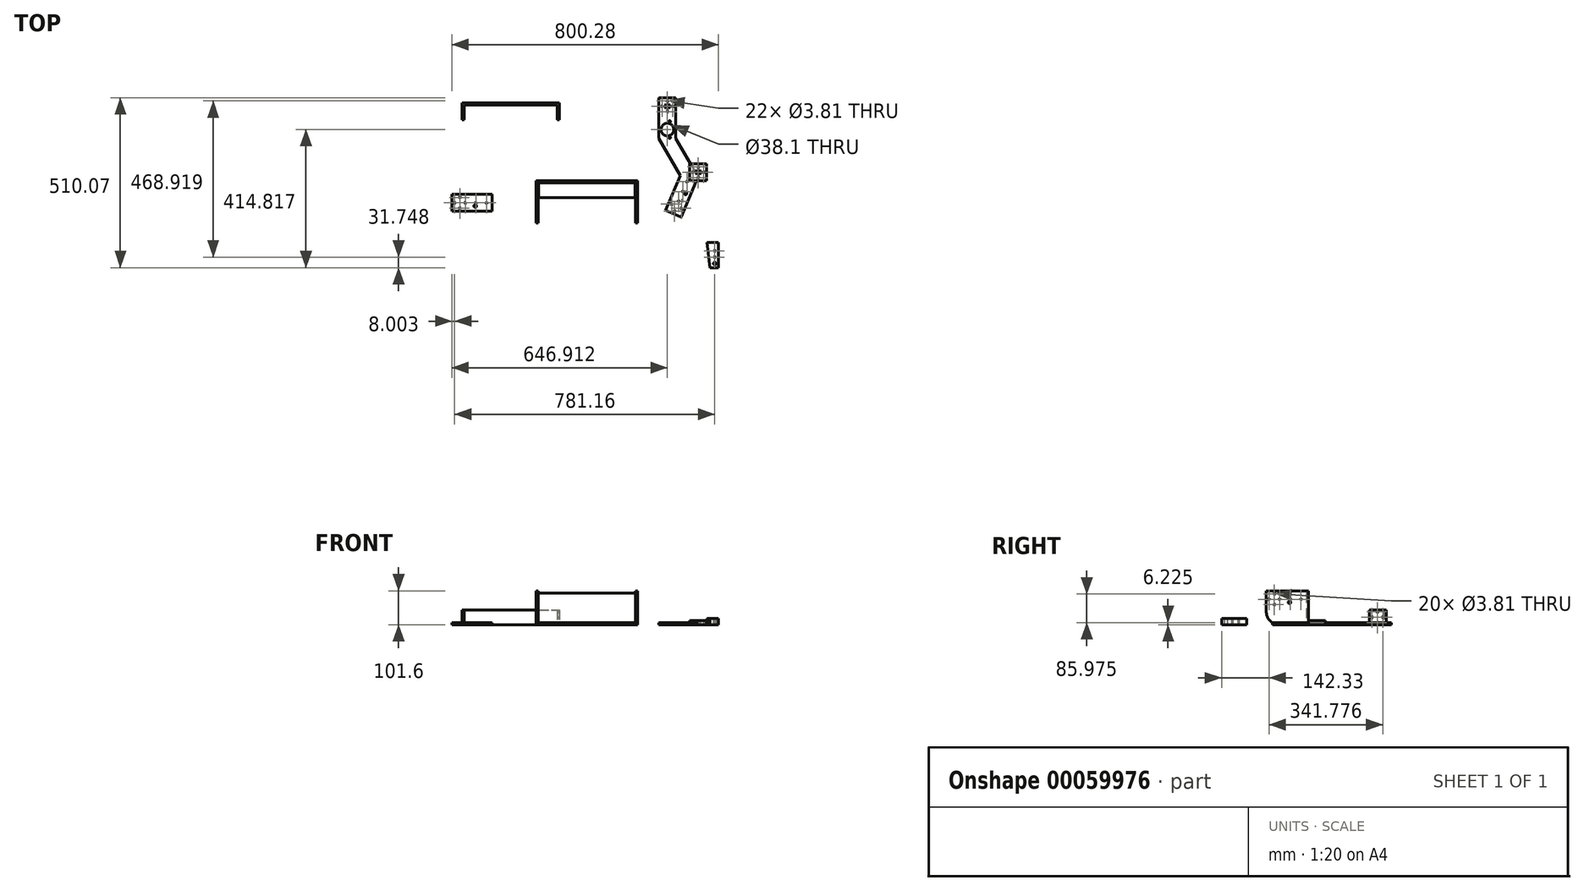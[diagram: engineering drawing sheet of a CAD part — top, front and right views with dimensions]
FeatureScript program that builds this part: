
annotation { "Feature Type Name" : "Feature", "Feature Type Description" : "" }
export const myFeature = defineFeature(function(context is Context, id is Id, definition is map)
    precondition{}
    {
        {
            var Q0;
            Q0=qCreatedBy(makeId("Top.planeOp"),FACE);
            var sketch = newSketch(context, id + "F0", { "sketchPlane" : qUnion([Q0])});
            skLineSegment(sketch, "E0.bottom", {"start": v(-92.72, 248.74) * mm, "end": v(-41.92, 248.74) * mm});
            skLineSegment(sketch, "E0.left", {"start": v(-92.72, 248.74) * mm, "end": v(-92.72, 70.94) * mm});
            skLineSegment(sketch, "E0.right", {"start": v(-41.92, 248.74) * mm, "end": v(-41.92, 127.1) * mm});
            skPoint(sketch, "E1.centerSnap0", {"position": v(-67.32, 248.74) * mm});
            skCircle(sketch, "E2", {"center": v(-67.32, 153.49) * mm, "radius": 19.05 * mm});
            skCircle(sketch, "E3", {"center": v(-67.32, 239.34) * mm, "radius": 1.9 * mm});
            skLineSegment(sketch, "E4", {"start": v(-67.32, 153.49) * mm, "end": v(-41.92, 153.49) * mm, "construction": true});
            skCircle(sketch, "E5", {"center": v(-60.82, 177.49) * mm, "radius": 2.7 * mm});
            skCircle(sketch, "E6.MirrorC", {"center": v(-60.82, 129.49) * mm, "radius": 2.7 * mm});
            skCircle(sketch, "E7.1.0", {"center": v(-83.32, 223.34) * mm, "radius": 1.9 * mm});
            skCircle(sketch, "E7.2.0", {"center": v(-67.32, 207.34) * mm, "radius": 1.9 * mm});
            skCircle(sketch, "E7.3.0", {"center": v(-51.32, 223.34) * mm, "radius": 1.9 * mm});
            skPoint(sketch, "E7.center", {"position": v(-67.32, 223.34) * mm});
            skLineSegment(sketch, "E8", {"start": v(14.65, -13.3) * mm, "end": v(14.65, -13.3) * mm});
            skLineSegment(sketch, "E9", {"start": v(14.65, -13.3) * mm, "end": v(-25.75, -108.67) * mm});
            skLineSegment(sketch, "E10", {"start": v(-25.75, -108.67) * mm, "end": v(-72.52, -88.86) * mm});
            skLineSegment(sketch, "E11", {"start": v(14.65, -13.3) * mm, "end": v(14.65, -108.56) * mm, "construction": true});
            skLineSegment(sketch, "E12", {"start": v(-72.52, -88.86) * mm, "end": v(-48.43, -31.97) * mm});
            skLineSegment(sketch, "E13", {"start": v(-48.43, -31.97) * mm, "end": v(-42.25, -17.39) * mm});
            skLineSegment(sketch, "E14", {"start": v(14.65, -13.3) * mm, "end": v(18.79, -3.55) * mm});
            skLineSegment(sketch, "E15", {"start": v(-42.25, -17.39) * mm, "end": v(-28.58, 14.87) * mm});
            skCircle(sketch, "E16.cCircle", {"center": v(-67.32, 223.34) * mm, "radius": 6.35 * mm, "construction": true});
            skLineSegment(sketch, "E16.0", {"start": v(-70.98, 229.69) * mm, "end": v(-63.65, 229.69) * mm});
            skLineSegment(sketch, "E16.1", {"start": v(-63.65, 229.69) * mm, "end": v(-59.99, 223.34) * mm});
            skLineSegment(sketch, "E16.2", {"start": v(-59.99, 223.34) * mm, "end": v(-63.65, 216.99) * mm});
            skLineSegment(sketch, "E16.3", {"start": v(-63.65, 216.99) * mm, "end": v(-70.98, 216.99) * mm});
            skLineSegment(sketch, "E16.4", {"start": v(-70.98, 216.99) * mm, "end": v(-74.65, 223.34) * mm});
            skLineSegment(sketch, "E16.5", {"start": v(-74.65, 223.34) * mm, "end": v(-70.98, 229.69) * mm});
            skPoint(sketch, "E16.0.midPoint", {"position": v(-67.32, 229.69) * mm});
            skLineSegment(sketch, "E17", {"start": v(-28.58, 14.87) * mm, "end": v(-28.58, 14.87) * mm});
            skLineSegment(sketch, "E18", {"start": v(-28.58, 14.87) * mm, "end": v(-92.72, 127.1) * mm});
            skLineSegment(sketch, "E19", {"start": v(-41.92, 127.1) * mm, "end": v(24.73, 10.48) * mm});
            skLineSegment(sketch, "E20", {"start": v(24.73, 10.48) * mm, "end": v(18.79, -3.55) * mm});
            skPoint(sketch, "E21.start.orphan", {"position": v(-92.72, 102.69) * mm});
            skPoint(sketch, "E22.orphan", {"position": v(-41.92, 102.69) * mm});
            skSolve(sketch);
        }
        {
            var Q0;
            {var subQ0=sQuery(id+"F0.wireOp",EDGE,"9e544ab8-24b0-4bfb-8a0b-cb48c2a7bfe7.right");Q0=makeQuery(id+"F0.imprint","IMPRINT",FACE,{"disambiguationData":[TD([[makeQuery(id+"F0.imprint","IMPRINT",EDGE,{"derivedFrom":subQ0}),-1.0]])]});}
            var Q1;
            {var subQ6=sQuery(id+"F0.wireOp",EDGE,"E0.bottom");Q1=makeQuery(id+"F0.imprint","IMPRINT",FACE,{"disambiguationData":[TD([[makeQuery(id+"F0.imprint","IMPRINT",EDGE,{"derivedFrom":subQ6}),-1.0]])]});}
            var Q2;
            {var subQ5=sQuery(id+"F0.wireOp",EDGE,"rFdDuM6M-3oRl-HpnY-bc0J-Wi5shL16RlnQ");Q2=makeQuery(id+"F0.imprint","IMPRINT",FACE,{"disambiguationData":[TD([[makeQuery(id+"F0.imprint","IMPRINT",EDGE,{"derivedFrom":subQ5}),-1.0]])]});}
            var Q3;
            {var subQ0=sQuery(id+"F0.wireOp",EDGE,"E10");Q3=makeQuery(id+"F0.imprint","IMPRINT",FACE,{"disambiguationData":[TD([[makeQuery(id+"F0.imprint","IMPRINT",EDGE,{"derivedFrom":subQ0}),-1.0]])]});}
            var Q4;
            {var subQ0=sQuery(id+"F0.wireOp",EDGE,"00836efd-f910-459f-9125-7ec244fb97d2.trimOffspring");Q4=makeQuery(id+"F0.imprint","IMPRINT",FACE,{"disambiguationData":[TD([[makeQuery(id+"F0.imprint","IMPRINT",EDGE,{"derivedFrom":subQ0}),-1.0]])]});}
            extrude(context, id + "F1", {"entities" : qUnion([Q0, Q1, Q2, Q3, Q4]), "depth" : 6.35 * mm});
        }
        {
            var Q0;
            Q0=qCreatedBy(makeId("Top.planeOp"),FACE);
            var sketch = newSketch(context, id + "F2", { "sketchPlane" : qUnion([Q0])});
            skLineSegment(sketch, "E23.bottom", {"start": v(0, 0) * mm, "end": v(50.8, 0) * mm});
            skLineSegment(sketch, "E23.top", {"start": v(0, 50.8) * mm, "end": v(50.8, 50.8) * mm});
            skLineSegment(sketch, "E23.left", {"start": v(0, 0) * mm, "end": v(0, 50.8) * mm});
            skLineSegment(sketch, "E23.right", {"start": v(50.8, 0) * mm, "end": v(50.8, 50.8) * mm});
            skCircle(sketch, "E24.cCircle", {"center": v(25.4, 25.4) * mm, "radius": 6.35 * mm, "construction": true});
            skPoint(sketch, "E24.cCircle.centerSnap0", {"position": v(0, 25.4) * mm});
            skPoint(sketch, "E24.cCircle.centerSnap1", {"position": v(25.4, 0) * mm});
            skLineSegment(sketch, "E24.0", {"start": v(21.73, 31.75) * mm, "end": v(29.07, 31.75) * mm});
            skLineSegment(sketch, "E24.1", {"start": v(29.07, 31.75) * mm, "end": v(32.73, 25.4) * mm});
            skLineSegment(sketch, "E24.2", {"start": v(32.73, 25.4) * mm, "end": v(29.07, 19.05) * mm});
            skLineSegment(sketch, "E24.3", {"start": v(29.07, 19.05) * mm, "end": v(21.73, 19.05) * mm});
            skLineSegment(sketch, "E24.4", {"start": v(21.73, 19.05) * mm, "end": v(18.07, 25.4) * mm});
            skLineSegment(sketch, "E24.5", {"start": v(18.07, 25.4) * mm, "end": v(21.73, 31.75) * mm});
            skPoint(sketch, "E24.0.midPoint", {"position": v(25.4, 31.75) * mm});
            skCircle(sketch, "E25", {"center": v(25.4, 41.4) * mm, "radius": 1.9 * mm});
            skCircle(sketch, "E26.1.0", {"center": v(9.4, 25.4) * mm, "radius": 1.9 * mm});
            skCircle(sketch, "E26.2.0", {"center": v(25.4, 9.4) * mm, "radius": 1.9 * mm});
            skCircle(sketch, "E26.3.0", {"center": v(41.4, 25.4) * mm, "radius": 1.9 * mm});
            skSolve(sketch);
        }
        {
            var Q0;
            Q0=makeQuery(id+"F2.imprint","IMPRINT",FACE,{"disambiguationData":[TD([[makeQuery(id+"F2.imprint","IMPRINT",EDGE,{"derivedFrom":sQuery(id+"F2.wireOp",EDGE,"E23.bottom")}),1.0]])]});
            extrude(context, id + "F3", {"entities" : qUnion([Q0]), "depth" : 12.7 * mm});
        }
        {
            var Q0;
            Q0=qCreatedBy(makeId("Top.planeOp"),FACE);
            var sketch = newSketch(context, id + "F4", { "sketchPlane" : qUnion([Q0])});
            skLineSegment(sketch, "E27.bottom", {"start": v(35.25, -261.33) * mm, "end": v(86.05, -261.33) * mm});
            skLineSegment(sketch, "E27.top", {"start": v(35.25, -185.13) * mm, "end": v(86.05, -185.13) * mm});
            skLineSegment(sketch, "E27.left", {"start": v(35.25, -261.33) * mm, "end": v(35.25, -185.13) * mm});
            skLineSegment(sketch, "E27.right", {"start": v(86.05, -261.33) * mm, "end": v(86.05, -185.13) * mm});
            skCircle(sketch, "E28", {"center": v(74.93, -248.63) * mm, "radius": 3.97 * mm});
            skCircle(sketch, "E29", {"center": v(74.93, -229.58) * mm, "radius": 1.9 * mm});
            skCircle(sketch, "E30", {"center": v(74.93, -210.53) * mm, "radius": 1.9 * mm});
            skLineSegment(sketch, "E31", {"start": v(60.65, -261.33) * mm, "end": v(51.96, -185.13) * mm});
            skSolve(sketch);
        }
        {
            var Q0;
            {var subQ0=sQuery(id+"F4.wireOp",EDGE,"E27.right");Q0=makeQuery(id+"F4.imprint","IMPRINT",FACE,{"disambiguationData":[TD([[makeQuery(id+"F4.imprint","IMPRINT",EDGE,{"derivedFrom":subQ0}),1.0]])]});}
            extrude(context, id + "F5", {"entities" : qUnion([Q0]), "depth" : 19.05 * mm});
        }
        {
            var Q0;
            Q0=qCreatedBy(makeId("Front.planeOp"),FACE);
            var sketch = newSketch(context, id + "F6", { "sketchPlane" : qUnion([Q0])});
            skLineSegment(sketch, "E32.bottom", {"start": v(-156.94, 0) * mm, "end": v(-461.74, 0) * mm});
            skLineSegment(sketch, "E32.top", {"start": v(-156.94, 101.6) * mm, "end": v(-461.74, 101.6) * mm});
            skLineSegment(sketch, "E32.left", {"start": v(-156.94, 0) * mm, "end": v(-156.94, 101.6) * mm});
            skLineSegment(sketch, "E32.right", {"start": v(-461.74, 0) * mm, "end": v(-461.74, 101.6) * mm});
            skLineSegment(sketch, "E33.bottom", {"start": v(-461.74, 101.6) * mm, "end": v(-455.4, 101.6) * mm});
            skLineSegment(sketch, "E33.top", {"start": v(-461.74, 0) * mm, "end": v(-455.4, 0) * mm});
            skLineSegment(sketch, "E33.left", {"start": v(-461.74, 101.6) * mm, "end": v(-461.74, 0) * mm});
            skLineSegment(sketch, "E34.bottom", {"start": v(-156.94, 0) * mm, "end": v(-163.3, 0) * mm});
            skLineSegment(sketch, "E34.top", {"start": v(-156.94, 101.6) * mm, "end": v(-163.3, 101.6) * mm});
            skSolve(sketch);
        }
        {
            var Q0;
            Q0=makeQuery(id+"F6.imprint","IMPRINT",FACE,{"disambiguationData":[TD([[makeQuery(id+"F6.imprint","IMPRINT",EDGE,{"derivedFrom":sQuery(id+"F6.wireOp",EDGE,"E32.bottom")}),-1.0]])]});
            var Q1;
            Q1=makeQuery(id+"F6.imprint","IMPRINT",FACE,{"disambiguationData":[TD([[makeQuery(id+"F6.imprint","IMPRINT",EDGE,{"derivedFrom":sQuery(id+"F6.wireOp",EDGE,"E33.bottom")}),-1.0]])]});
            var Q2;
            Q2=makeQuery(id+"F6.imprint","IMPRINT",FACE,{"disambiguationData":[TD([[makeQuery(id+"F6.imprint","IMPRINT",EDGE,{"derivedFrom":sQuery(id+"F6.wireOp",EDGE,"E34.bottom")}),-1.0]])]});
            extrude(context, id + "F7", {"entities" : qUnion([Q0, Q1, Q2]), "depth" : 6.35 * mm});
        }
        {
            var Q0;
            Q0=makeQuery(id+"F7.opExtrude","CAP_FACE",FACE,{"disambiguationData":[OSD([sQuery(id+"F6.wireOp",EDGE,"E32.bottom"),sQuery(id+"F6.wireOp",EDGE,"E32.top"),sQuery(id+"F6.wireOp",EDGE,"E33.bottom"),sQuery(id+"F6.wireOp",EDGE,"E33.top"),sQuery(id+"F6.wireOp",EDGE,"E33.left"),sQuery(id+"F6.wireOp",EDGE,"E34.bottom"),sQuery(id+"F6.wireOp",EDGE,"E34.top"),sQuery(id+"F6.wireOp",EDGE,"E32.left")])],"isStart":false});
            var sketch = newSketch(context, id + "F8", { "sketchPlane" : qUnion([Q0])});
            skLineSegment(sketch, "E35.bottom", {"start": v(-461.74, 101.6) * mm, "end": v(-455.4, 101.6) * mm});
            skLineSegment(sketch, "E35.top", {"start": v(-461.74, 0) * mm, "end": v(-455.4, 0) * mm});
            skLineSegment(sketch, "E35.left", {"start": v(-461.74, 101.6) * mm, "end": v(-461.74, 0) * mm});
            skLineSegment(sketch, "E35.right", {"start": v(-455.4, 101.6) * mm, "end": v(-455.4, 0) * mm});
            skLineSegment(sketch, "E36.bottom", {"start": v(-156.94, 101.6) * mm, "end": v(-163.3, 101.6) * mm});
            skLineSegment(sketch, "E36.top", {"start": v(-156.94, 0) * mm, "end": v(-163.3, 0) * mm});
            skLineSegment(sketch, "E36.left", {"start": v(-156.94, 101.6) * mm, "end": v(-156.94, 0) * mm});
            skLineSegment(sketch, "E36.right", {"start": v(-163.3, 101.6) * mm, "end": v(-163.3, 0) * mm});
            skSolve(sketch);
        }
        {
            var Q0;
            Q0 = qSketchRegion(id + "F8", true);
            extrude(context, id + "F9", {"entities" : qUnion([Q0]), "operationType" : NewBodyOperationType.ADD, "depth" : 120.65 * mm});
        }
        {
            var Q0;
            Q0=makeQuery(id+"F7.opExtrude","CAP_FACE",FACE,{"disambiguationData":[OSD([sQuery(id+"F6.wireOp",EDGE,"E32.bottom"),sQuery(id+"F6.wireOp",EDGE,"E32.top"),sQuery(id+"F6.wireOp",EDGE,"E33.bottom"),sQuery(id+"F6.wireOp",EDGE,"E33.top"),sQuery(id+"F6.wireOp",EDGE,"E33.left"),sQuery(id+"F6.wireOp",EDGE,"E34.bottom"),sQuery(id+"F6.wireOp",EDGE,"E34.top"),sQuery(id+"F6.wireOp",EDGE,"E32.left")])],"isStart":false});
            var sketch = newSketch(context, id + "F10", { "sketchPlane" : qUnion([Q0])});
            skPoint(sketch, "E37.oppositeSnap0", {"position": v(-309.34, 0) * mm});
            skLineSegment(sketch, "E37.bottom", {"start": v(-453.8, 0) * mm, "end": v(-309.34, 0) * mm});
            skLineSegment(sketch, "E37.top", {"start": v(-453.8, 6.35) * mm, "end": v(-309.34, 6.35) * mm});
            skLineSegment(sketch, "E37.left", {"start": v(-453.8, 0) * mm, "end": v(-453.8, 6.35) * mm});
            skLineSegment(sketch, "E37.right", {"start": v(-309.34, 0) * mm, "end": v(-309.34, 6.35) * mm});
            skLineSegment(sketch, "E38.MirrorCS", {"start": v(-164.88, 6.35) * mm, "end": v(-309.34, 6.35) * mm});
            skLineSegment(sketch, "E39.MirrorCS", {"start": v(-164.88, 0) * mm, "end": v(-164.88, 6.35) * mm});
            skSolve(sketch);
        }
        {
            var Q0;
            Q0 = qSketchRegion(id + "F10", true);
            var Q1;
            {var subQ0=sQuery(id+"F10.wireOp",EDGE,"E37.right");Q1=makeQuery(id+"F10.imprint","IMPRINT",FACE,{"disambiguationData":[TD([[makeQuery(id+"F10.imprint","IMPRINT",EDGE,{"derivedFrom":subQ0}),-1.0]])]});}
            extrude(context, id + "F11", {"entities" : qUnion([Q0, Q1]), "operationType" : NewBodyOperationType.ADD, "depth" : 44.45 * mm});
        }
        {
            var Q0;
            Q0=makeQuery(id+"F9.boolean.opBoolean","MERGE",FACE,{"derivedFrom":[makeQuery(id+"F7.opExtrude","SWEPT_FACE",FACE,{"disambiguationData":[OSD([sQuery(id+"F6.wireOp",EDGE,"E32.left")])]}),makeQuery(id+"F9.opExtrude","SWEPT_FACE",FACE,{"disambiguationData":[OSD([sQuery(id+"F8.wireOp",EDGE,"E36.left")])]})]});
            var sketch = newSketch(context, id + "F12", { "sketchPlane" : qUnion([Q0])});
            skCircle(sketch, "E40", {"center": v(-57.15, 66.68) * mm, "radius": 3.97 * mm});
            skLineSegment(sketch, "E41", {"start": v(-127, 76.2) * mm, "end": v(0, 76.2) * mm, "construction": true});
            skCircle(sketch, "E42", {"center": v(-103, 76.2) * mm, "radius": 16 * mm, "construction": true});
            skCircle(sketch, "E43", {"center": v(-119, 76.2) * mm, "radius": 1.9 * mm});
            skCircle(sketch, "E44", {"center": v(-103, 92.2) * mm, "radius": 1.9 * mm});
            skCircle(sketch, "E45", {"center": v(-103, 60.2) * mm, "radius": 1.9 * mm});
            skCircle(sketch, "E46", {"center": v(-87, 76.2) * mm, "radius": 1.9 * mm});
            skCircle(sketch, "E47", {"center": v(-55, 76.2) * mm, "radius": 1.9 * mm});
            skCircle(sketch, "E48", {"center": v(-23, 76.2) * mm, "radius": 1.9 * mm});
            skArc(sketch, "E49", {"start": v(-127, 38.1) * mm, "mid": v(-115.59, 11.41) * mm, "end": v(-88.9, 0) * mm});
            skSolve(sketch);
        }
        {
            var Q0;
            Q0=qCreatedBy(makeId("Top.planeOp"),FACE);
            var sketch = newSketch(context, id + "F13", { "sketchPlane" : qUnion([Q0])});
            skLineSegment(sketch, "E50.bottom", {"start": v(-684.13, 233.58) * mm, "end": v(-392.03, 233.58) * mm});
            skLineSegment(sketch, "E50.top", {"start": v(-684.13, 182.78) * mm, "end": v(-392.03, 182.78) * mm});
            skLineSegment(sketch, "E50.left", {"start": v(-684.13, 233.58) * mm, "end": v(-684.13, 182.78) * mm});
            skLineSegment(sketch, "E50.right", {"start": v(-392.03, 233.58) * mm, "end": v(-392.03, 182.78) * mm});
            skLineSegment(sketch, "E51.bottom", {"start": v(-677.78, 182.78) * mm, "end": v(-398.38, 182.78) * mm});
            skLineSegment(sketch, "E51.top", {"start": v(-677.78, 227.23) * mm, "end": v(-398.38, 227.23) * mm});
            skLineSegment(sketch, "E51.left", {"start": v(-677.78, 182.78) * mm, "end": v(-677.78, 227.23) * mm});
            skLineSegment(sketch, "E51.right", {"start": v(-398.38, 182.78) * mm, "end": v(-398.38, 227.23) * mm});
            skSolve(sketch);
        }
        {
            var Q0;
            Q0=makeQuery(id+"F13.imprint","IMPRINT",FACE,{"disambiguationData":[TD([[makeQuery(id+"F13.imprint","IMPRINT",EDGE,{"derivedFrom":sQuery(id+"F13.wireOp",EDGE,"E50.bottom")}),-1.0]])]});
            extrude(context, id + "F14", {"entities" : qUnion([Q0]), "depth" : 44.45 * mm});
        }
        {
            var Q0;
            Q0 = qSketchRegion(id + "F12", true);
            var Q1;
            {var subQ0=sQuery(id+"F12.wireOp",EDGE,"E49");Q1=makeQuery(id+"F12.imprint","IMPRINT",FACE,{"disambiguationData":[TD([[makeQuery(id+"F12.imprint","IMPRINT",EDGE,{"derivedFrom":subQ0}),-1.0]])]});}
            extrude(context, id + "F15", {"entities" : qUnion([Q0, Q1]), "operationType" : NewBodyOperationType.REMOVE, "endBound" : BoundingType.THROUGH_ALL, "oppositeDirection" : true, "depth" : 25.4 * mm});
        }
        {
            var Q0;
            Q0=makeQuery(id+"F1.opExtrude","CAP_FACE",FACE,{"disambiguationData":[OSD([sQuery(id+"F0.wireOp",EDGE,"E0.bottom"),sQuery(id+"F0.wireOp",EDGE,"E0.left"),sQuery(id+"F0.wireOp",EDGE,"E0.right"),sQuery(id+"F0.wireOp",EDGE,"E1"),sQuery(id+"F0.wireOp",EDGE,"E2"),sQuery(id+"F0.wireOp",EDGE,"E3"),sQuery(id+"F0.wireOp",EDGE,"E5"),sQuery(id+"F0.wireOp",EDGE,"E6.MirrorC"),sQuery(id+"F0.wireOp",EDGE,"E7.1.0"),sQuery(id+"F0.wireOp",EDGE,"E7.2.0"),sQuery(id+"F0.wireOp",EDGE,"E7.3.0"),sQuery(id+"F0.wireOp",EDGE,"E9"),sQuery(id+"F0.wireOp",EDGE,"E10"),sQuery(id+"F0.wireOp",EDGE,"E12"),sQuery(id+"F0.wireOp",EDGE,"E13"),sQuery(id+"F0.wireOp",EDGE,"yjABQQOX-nqtP-5HEc-Mw7k-6ywUgyRkbhnT"),sQuery(id+"F0.wireOp",EDGE,"E14"),sQuery(id+"F0.wireOp",EDGE,"E21"),sQuery(id+"F0.wireOp",EDGE,"E15")])],"isStart":false});
            var sketch = newSketch(context, id + "F16", { "sketchPlane" : qUnion([Q0])});
            skCircle(sketch, "E52", {"center": v(-13.12, -38.16) * mm, "radius": 3.97 * mm});
            skLineSegment(sketch, "E53", {"start": v(-49.14, -98.77) * mm, "end": v(-30.41, -54.57) * mm, "construction": true});
            skCircle(sketch, "E54", {"center": v(-46.02, -91.4) * mm, "radius": 1.9 * mm});
            skCircle(sketch, "E55", {"center": v(-33.53, -61.93) * mm, "radius": 1.9 * mm});
            skLineSegment(sketch, "E56", {"start": v(-25.04, -82.9) * mm, "end": v(-54.5, -70.43) * mm, "construction": true});
            skCircle(sketch, "E57", {"center": v(-54.5, -70.43) * mm, "radius": 1.9 * mm});
            skCircle(sketch, "E58", {"center": v(-25.04, -82.9) * mm, "radius": 1.9 * mm});
            skPoint(sketch, "E59", {"position": v(-39.77, -76.67) * mm});
            skLineSegment(sketch, "E60", {"start": v(-30.41, -54.57) * mm, "end": v(-3.55, 8.83) * mm, "construction": true});
            skCircle(sketch, "E61", {"center": v(-21.05, -32.47) * mm, "radius": 1.9 * mm});
            skCircle(sketch, "E62", {"center": v(-8.57, -3) * mm, "radius": 1.9 * mm});
            skSolve(sketch);
        }
        {
            var Q0;
            Q0=makeQuery(id+"F14.opExtrude","SWEPT_FACE",FACE,{"disambiguationData":[OSD([sQuery(id+"F13.wireOp",EDGE,"E50.right")])]});
            var sketch = newSketch(context, id + "F17", { "sketchPlane" : qUnion([Q0])});
            skCircle(sketch, "E63", {"center": v(206.78, 22.23) * mm, "radius": 16 * mm, "construction": true});
            skPoint(sketch, "E63.centerSnap0", {"position": v(182.78, 22.23) * mm});
            skCircle(sketch, "E64", {"center": v(206.78, 38.22) * mm, "radius": 1.9 * mm});
            skCircle(sketch, "E65", {"center": v(206.78, 6.23) * mm, "radius": 1.9 * mm});
            skCircle(sketch, "E66", {"center": v(222.78, 22.23) * mm, "radius": 1.9 * mm});
            skCircle(sketch, "E67", {"center": v(190.78, 22.23) * mm, "radius": 1.9 * mm});
            skSolve(sketch);
        }
        {
            var Q0;
            Q0 = qSketchRegion(id + "F17", true);
            extrude(context, id + "F18", {"entities" : qUnion([Q0]), "operationType" : NewBodyOperationType.REMOVE, "endBound" : BoundingType.THROUGH_ALL, "oppositeDirection" : true, "depth" : 25.4 * mm});
        }
        {
            var Q0;
            Q0 = qSketchRegion(id + "F16", true);
            var Q1;
            Q1=sQuery(id+"F16.wireOp",EDGE,"E52");
            extrude(context, id + "F19", {"entities" : qUnion([Q0]), "operationType" : NewBodyOperationType.REMOVE, "surfaceEntities" : qUnion([Q1]), "endBound" : BoundingType.UP_TO_NEXT, "oppositeDirection" : true, "depth" : 25.4 * mm});
        }
        {
            var Q0;
            Q0=qCreatedBy(makeId("Top.planeOp"),FACE);
            var sketch = newSketch(context, id + "F20", { "sketchPlane" : qUnion([Q0])});
            skLineSegment(sketch, "E68.bottom", {"start": v(-714.23, -91.9) * mm, "end": v(-593.58, -91.9) * mm});
            skLineSegment(sketch, "E68.top", {"start": v(-714.23, -41.1) * mm, "end": v(-593.58, -41.1) * mm});
            skLineSegment(sketch, "E68.left", {"start": v(-714.23, -91.9) * mm, "end": v(-714.23, -41.1) * mm});
            skLineSegment(sketch, "E68.right", {"start": v(-593.58, -91.9) * mm, "end": v(-593.58, -41.1) * mm});
            skCircle(sketch, "E69", {"center": v(-690.23, -66.5) * mm, "radius": 16 * mm, "construction": true});
            skPoint(sketch, "E69.centerSnap0", {"position": v(-714.23, -66.5) * mm});
            skCircle(sketch, "E70", {"center": v(-690.23, -50.5) * mm, "radius": 1.9 * mm});
            skCircle(sketch, "E71", {"center": v(-674.23, -66.5) * mm, "radius": 1.9 * mm});
            skCircle(sketch, "E72", {"center": v(-706.23, -66.5) * mm, "radius": 1.9 * mm});
            skCircle(sketch, "E73", {"center": v(-690.23, -82.5) * mm, "radius": 1.9 * mm});
            skCircle(sketch, "E74", {"center": v(-642.23, -66.5) * mm, "radius": 1.9 * mm});
            skCircle(sketch, "E75", {"center": v(-610.23, -66.5) * mm, "radius": 1.9 * mm});
            skCircle(sketch, "E76", {"center": v(-644.38, -76.02) * mm, "radius": 3.97 * mm});
            skSolve(sketch);
        }
        {
            var Q0;
            Q0=makeQuery(id+"F20.imprint","IMPRINT",FACE,{"disambiguationData":[TD([[makeQuery(id+"F20.imprint","IMPRINT",EDGE,{"derivedFrom":sQuery(id+"F20.wireOp",EDGE,"E68.bottom")}),1.0]])]});
            extrude(context, id + "F21", {"entities" : qUnion([Q0]), "depth" : 6.35 * mm});
        }
        {
            var Q0;
            Q0=makeQuery(id+"F7.opExtrude","CAP_FACE",FACE,{"disambiguationData":[OSD([sQuery(id+"F6.wireOp",EDGE,"E32.bottom"),sQuery(id+"F6.wireOp",EDGE,"E32.top"),sQuery(id+"F6.wireOp",EDGE,"E33.bottom"),sQuery(id+"F6.wireOp",EDGE,"E33.top"),sQuery(id+"F6.wireOp",EDGE,"E33.left"),sQuery(id+"F6.wireOp",EDGE,"E34.bottom"),sQuery(id+"F6.wireOp",EDGE,"E34.top"),sQuery(id+"F6.wireOp",EDGE,"E32.left")])],"isStart":true});
            var sketch = newSketch(context, id + "F22", { "sketchPlane" : qUnion([Q0])});
            skLineSegment(sketch, "E77.bottom", {"start": v(163.3, 101.6) * mm, "end": v(455.4, 101.6) * mm});
            skLineSegment(sketch, "E77.top", {"start": v(163.3, 95.25) * mm, "end": v(455.4, 95.25) * mm});
            skLineSegment(sketch, "E77.left", {"start": v(163.3, 101.6) * mm, "end": v(163.3, 95.25) * mm});
            skLineSegment(sketch, "E77.right", {"start": v(455.4, 101.6) * mm, "end": v(455.4, 95.25) * mm});
            skSolve(sketch);
        }
        {
            var Q0;
            Q0=makeQuery(id+"F22.imprint","IMPRINT",FACE,{"disambiguationData":[TD([[makeQuery(id+"F22.imprint","IMPRINT",EDGE,{"derivedFrom":sQuery(id+"F22.wireOp",EDGE,"E77.bottom")}),-1.0]])]});
            extrude(context, id + "F23", {"entities" : qUnion([Q0]), "operationType" : NewBodyOperationType.REMOVE, "endBound" : BoundingType.UP_TO_NEXT, "oppositeDirection" : true, "depth" : 25.4 * mm});
        }
    });
